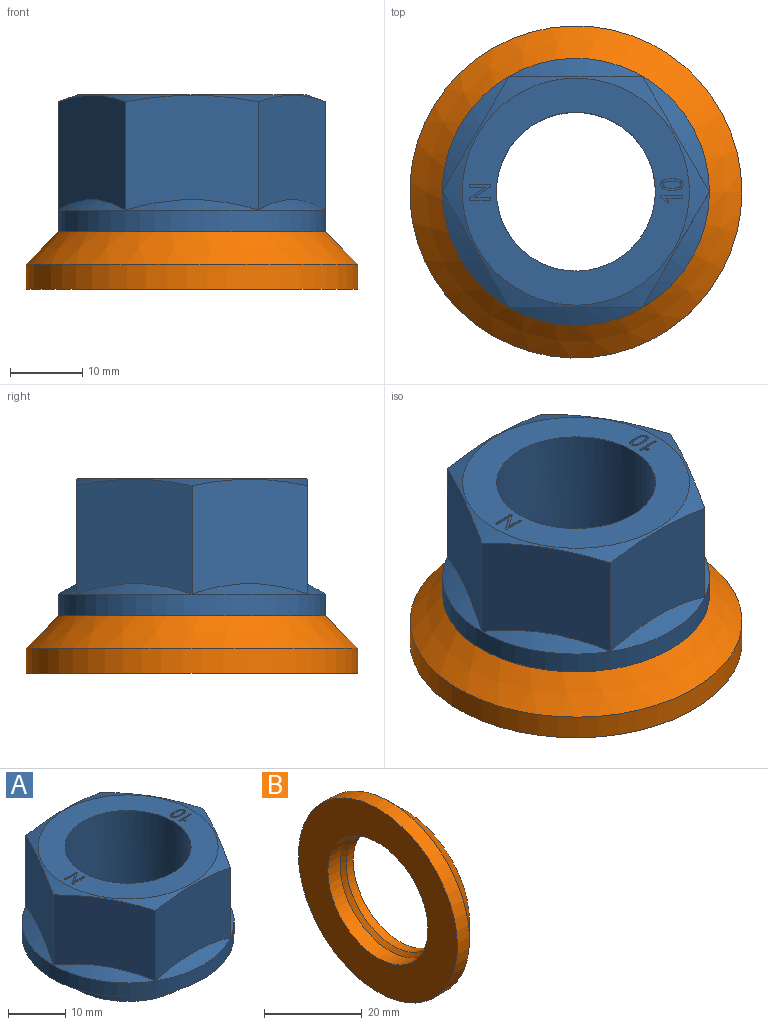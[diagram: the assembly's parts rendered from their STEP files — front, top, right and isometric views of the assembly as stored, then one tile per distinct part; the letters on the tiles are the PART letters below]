
ASSEMBLY  parts=2 mates=1
PART A: 50 faces, bbox 37x37x24.4 mm
  f0: extruded ~1.23x0.48mm, area 0.4mm2, adj f1,f3,f9,f49
  f1: extruded ~1.23x0.5mm, area 0.4mm2, adj f0,f2,f9,f49
  f2: extruded ~1.23x0.48mm, area 0.4mm2, adj f1,f3,f9,f49
  f3: extruded ~1.23x0.5mm, area 0.4mm2, adj f0,f2,f9,f49
  f4: extruded ~1.53x0.8mm, area 0.5mm2, adj f5,f8,f9,f33
  f5: extruded ~1.53x0.8mm, area 0.5mm2, adj f4,f6,f9,f33
  f6: extruded ~1.22x0.25mm, area 0.3mm2, adj f5,f7,f9,f33
  f7: extruded ~0.56x0.32mm, area 0.2mm2, adj f6,f8,f9,f33
  f8: extruded ~1.53x0.8mm, area 0.5mm2, adj f4,f7,f9,f33
  f9: plane 3.06x1.61mm, normal (0,0,1), area 2mm2, adj f0,f1,f2,f3,f4,f5,f6,f7
  f10: plane 2.63x0.25mm, normal (0,1,0), area 0.7mm2, adj f11,f23,f24,f33
  f11: extruded ~0.25x0.19mm, area 0.1mm2, adj f10,f12,f24,f33
  f12: extruded ~0.25x0.19mm, area 0.1mm2, adj f11,f13,f24,f33
  f13: plane 2.03x0.25mm, normal (0,-1,0), area 0.5mm2, adj f12,f14,f24,f33
  f14: plane 2.11x1.45mm, normal (-0.57,0.82,0), area 0.6mm2, adj f13,f15,f24,f33
  f15: extruded ~0.25x0.2mm, area 0.1mm2, adj f14,f16,f24,f33
  f16: extruded ~0.25x0.18mm, area 0.1mm2, adj f15,f17,f24,f33
  f17: plane 2.64x0.25mm, normal (0,-1,0), area 0.7mm2, adj f16,f18,f24,f33
  f18: extruded ~0.25x0.19mm, area 0.1mm2, adj f17,f19,f24,f33
  f19: extruded ~0.25x0.19mm, area 0.1mm2, adj f18,f20,f24,f33
  f20: plane 2.08x0.25mm, normal (0,1,0), area 0.5mm2, adj f19,f21,f24,f33
  f21: plane 2.14x1.47mm, normal (0.57,-0.83,0), area 0.6mm2, adj f20,f22,f24,f33
  f22: extruded ~0.25x0.2mm, area 0.1mm2, adj f21,f23,f24,f33
  f23: extruded ~0.25x0.18mm, area 0.1mm2, adj f10,f22,f24,f33
  f24: plane 3x2.17mm, normal (0,0,1), area 3mm2, adj f10,f11,f12,f13,f14,f15,f16,f17
  f25: plane 3.01x0.25mm, normal (0,-1,0), area 0.8mm2, adj f26,f31,f32,f33
  f26: plane 0.25x0.2mm, normal (1,0,0), area 0mm2, adj f25,f27,f32,f33
  f27: extruded ~0.75x0.71mm, area 0.3mm2, adj f26,f28,f32,f33
  f28: plane 0.36x0.25mm, normal (0,1,0), area 0.1mm2, adj f27,f29,f32,f33
  f29: extruded ~0.6x0.44mm, area 0.2mm2, adj f28,f30,f32,f33
  f30: plane 2.35x0.25mm, normal (0,1,0), area 0.6mm2, adj f29,f31,f32,f33
  f31: plane 0.3x0.25mm, normal (-1,0,0), area 0.1mm2, adj f25,f30,f32,f33
  f32: plane 3.01x0.91mm, normal (0,0,1), area 1.1mm2, adj f25,f26,f27,f28,f29,f30,f31
  f33: plane 31.46x31.46mm, normal (0,0,1), area 388.8mm2, adj f4,f5,f6,f7,f8,f10,f11,f12
  f34: cone r=17.1mm half-angle=70deg, axis (0,0,-1), area 116.7mm2, adj f33,f35,f36,f37,f38,f47,f48
  f35: plane 18.48x16.41mm, normal (0,-1,0), area 270.5mm2, adj f34,f36,f44,f48
  f36: plane 16.41x16mm, normal (-0.87,-0.5,0), area 270.5mm2, adj f34,f35,f37,f44
  f37: plane 16.41x16mm, normal (-0.87,0.5,0), area 270.5mm2, adj f34,f36,f38,f44
  f38: plane 18.48x16.41mm, normal (0,1,0), area 270.5mm2, adj f34,f37,f44,f47
  f39: plane 22.9x22.9mm, normal (0,0,-1), area 31.7mm2, adj f40,f46
  f40: cylinder r=11.45mm len=22.9mm, axis (0,0,1), area 287.8mm2, adj f39,f41
  f41: plane 25.5x25.5mm, normal (0,0,-1), area 98.8mm2, adj f40,f42
  f42: cylinder r=12.75mm len=25.5mm, axis (0,0,1), area 320.4mm2, adj f41,f43
  f43: cone r=15.62mm half-angle=80.1deg, axis (0,0,1), area 573mm2, adj f42,f45
  f44: cone r=14.75mm half-angle=60deg, axis (0,0,-1), area 217.5mm2, adj f35,f36,f37,f38,f45,f47,f48
  f45: cylinder r=18.5mm len=37mm, axis (0,0,-1), area 348.7mm2, adj f43,f44
  f46: cylinder r=11mm len=22mm, axis (0,0,1), area 1382.3mm2, adj f33,f39
  f47: plane 16.41x16mm, normal (0.87,0.5,0), area 270.5mm2, adj f34,f38,f44,f48
  f48: plane 16.41x16mm, normal (0.87,-0.5,0), area 270.5mm2, adj f34,f35,f44,f47
  f49: plane 2.46x0.98mm, normal (0,0,1), area 2mm2, adj f0,f1,f2,f3
PART B: 7 faces, bbox 8x46x46 mm
  f0: cone r=18.5mm half-angle=72deg, axis (1,0,0), area 519.6mm2, adj f1,f6
  f1: cone r=18.5mm half-angle=45deg, axis (-1,0,0), area 829.7mm2, adj f0,f2
  f2: cylinder r=23mm len=46mm, axis (1,0,0), area 505.8mm2, adj f1,f3
  f3: plane 46x46mm, normal (-1,0,0), area 1001.4mm2, adj f2,f4
  f4: cylinder r=14.5mm len=29mm, axis (1,0,0), area 319.6mm2, adj f3,f5
  f5: cone r=13.6mm half-angle=45deg, axis (-1,0,0), area 112.4mm2, adj f4,f6
  f6: cylinder r=13.6mm len=27.2mm, axis (1,0,0), area 170.9mm2, adj f0,f5
PLACE A t=(-6.03,0.43,16.44)mm
PLACE B rot(axis=(0,-1,0),90deg) t=(-6.03,0.43,13.44)mm
MATE slider B.f0 <-> A.f40  axis (0,0,1) through (-6.03,0.43,5.44)mm
